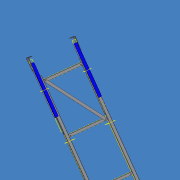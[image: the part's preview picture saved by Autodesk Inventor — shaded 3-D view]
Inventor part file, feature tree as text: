
AUTODESK INVENTOR PART (.ipt)
format: ipt  version: 2015 (Build 190159000, 159)  size: 74,752 bytes
history: native  units: mm
features: reference x2, extrude x1, sketch x1
ambient origin geometry x8: Origin, YZ Plane, XZ Plane, XY Plane, X Axis, Y Axis, Z Axis, Center Point
bodies: Solid1 (feature_tree)
feature tree (4):
  extrude  "Extrusion2"  Depth=30.0mm
  sketch  "Sketch1"  dims[d2=30.0mm d3=30.0mm d4=11.0mm d5=11.0mm d6=6.0mm d7=0.0mm]
  reference  "Reference1"
  reference  "Reference2"
